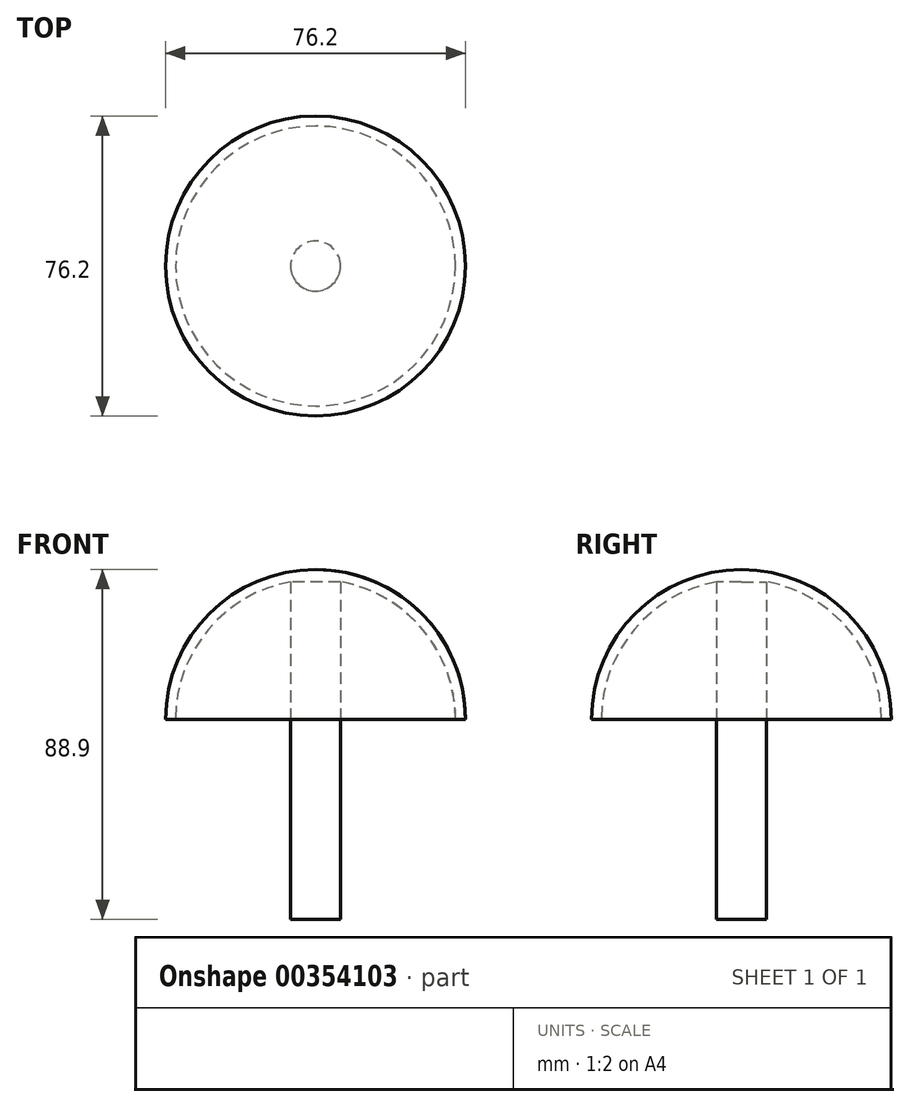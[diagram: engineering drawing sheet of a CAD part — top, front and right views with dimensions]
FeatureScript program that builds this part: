
annotation { "Feature Type Name" : "Feature", "Feature Type Description" : "" }
export const myFeature = defineFeature(function(context is Context, id is Id, definition is map)
    precondition{}
    {
        {
            var Q0;
            Q0=qCreatedBy(makeId("Top.planeOp"),FACE);
            var sketch = newSketch(context, id + "F0", { "sketchPlane" : qUnion([Q0])});
            skCircle(sketch, "E0", {"center": v(0, 0) * mm, "radius": 38.1 * mm});
            skSolve(sketch);
        }
        {
            var Q0;
            Q0=makeQuery(id+"F0.imprint","IMPRINT",FACE,{"disambiguationData":[TD([[makeQuery(id+"F0.imprint","IMPRINT",EDGE,{"derivedFrom":sQuery(id+"F0.wireOp",EDGE,"E0")}),1.0]])]});
            extrude(context, id + "F1", {"entities" : qUnion([Q0]), "depth" : 38.1 * mm});
        }
        {
            var Q0;
            Q0=makeQuery(id+"F1.opExtrude","CAP_FACE",FACE,{"disambiguationData":[OSD([sQuery(id+"F0.wireOp",EDGE,"E0")])],"isStart":false});
            fillet(context, id + "F2", {"entities" : qUnion([Q0]), "radius" : 38.1 * mm, "tangentPropagation" : true, "allowEdgeOverflow" : false});
        }
        {
            var Q0;
            Q0=makeQuery(id+"F1.opExtrude","CAP_FACE",FACE,{"disambiguationData":[OSD([sQuery(id+"F0.wireOp",EDGE,"E0")])],"isStart":true});
            shell(context, id + "F3", {"entities" : qUnion([Q0]), "thickness" : 2.54 * mm});
        }
        {
            var Q0;
            Q0=qCreatedBy(makeId("Top.planeOp"),FACE);
            var sketch = newSketch(context, id + "F4", { "sketchPlane" : qUnion([Q0])});
            skCircle(sketch, "E1", {"center": v(0, 0) * mm, "radius": 6.35 * mm});
            skSolve(sketch);
        }
        {
            var Q0;
            Q0 = qSketchRegion(id + "F4", true);
            extrude(context, id + "F5", {"entities" : qUnion([Q0]), "operationType" : NewBodyOperationType.ADD, "depth" : 35.56 * mm});
        }
        {
            var Q0;
            Q0=makeQuery(id+"F4.imprint","IMPRINT",FACE,{"disambiguationData":[TD([[makeQuery(id+"F4.imprint","IMPRINT",EDGE,{"derivedFrom":sQuery(id+"F4.wireOp",EDGE,"E1")}),1.0]])]});
            var Q1;
            Q1=sQuery(id+"F4.wireOp",EDGE,"E1");
            extrude(context, id + "F6", {"entities" : qUnion([Q0]), "surfaceEntities" : qUnion([Q1]), "oppositeDirection" : true, "depth" : 50.8 * mm});
        }
    });
